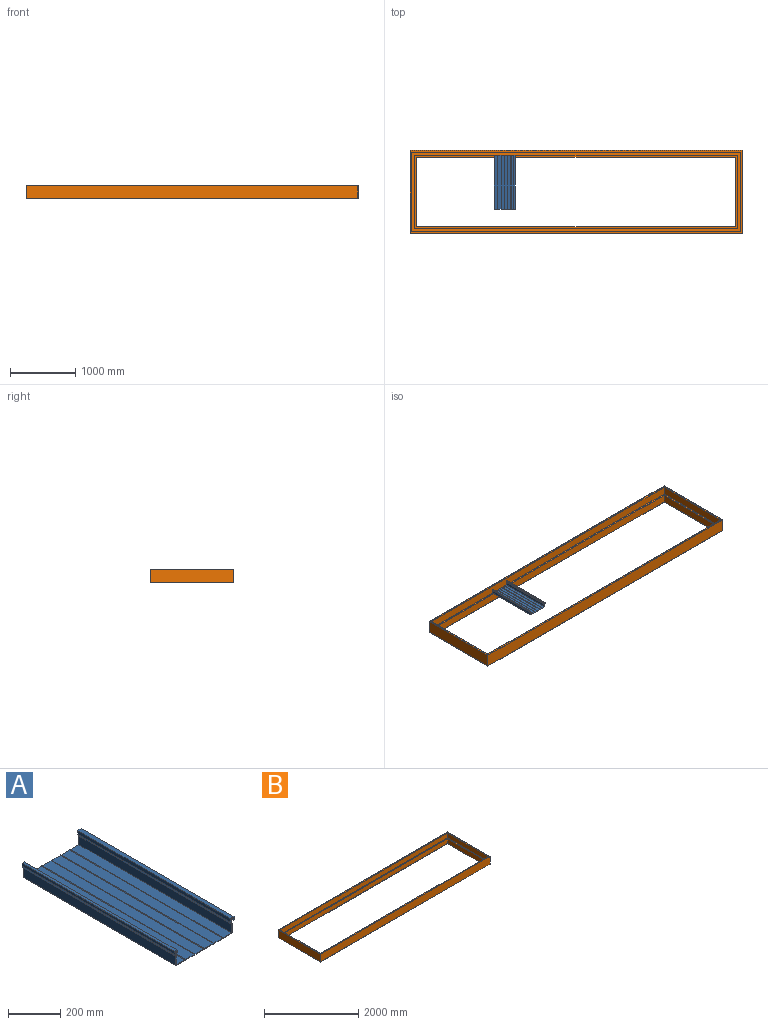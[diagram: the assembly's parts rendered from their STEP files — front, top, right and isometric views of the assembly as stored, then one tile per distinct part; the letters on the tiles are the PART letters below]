
ASSEMBLY  parts=2 mates=2
PART A: 58 faces, bbox 320.7x825.5x73 mm
  f0: plane 825.5x40.53mm, normal (-1,0,0), area 33453.8mm2, adj f1,f55,f56,f57
  f1: plane 825.5x46.04mm, normal (0,0,1), area 38004mm2, adj f0,f2,f56,f57
  f2: plane 825.5x1.59mm, normal (0.71,0,0.71), area 1853.3mm2, adj f1,f3,f56,f57
  f3: plane 825.5x1.59mm, normal (-0.71,0,0.71), area 1853.3mm2, adj f2,f4,f56,f57
  f4: plane 825.5x47.63mm, normal (0,0,1), area 39314.4mm2, adj f3,f5,f56,f57
  f5: plane 825.5x1.59mm, normal (0.71,0,0.71), area 1853.3mm2, adj f4,f6,f56,f57
  f6: plane 825.5x1.59mm, normal (-0.71,0,0.71), area 1853.3mm2, adj f5,f7,f56,f57
  f7: plane 825.5x47.63mm, normal (0,0,1), area 39314.4mm2, adj f6,f8,f56,f57
  f8: plane 825.5x1.59mm, normal (0.71,0,0.71), area 1853.3mm2, adj f7,f9,f56,f57
  f9: plane 825.5x1.59mm, normal (-0.71,0,0.71), area 1853.3mm2, adj f8,f10,f56,f57
  f10: plane 825.5x47.63mm, normal (0,0,1), area 39314.4mm2, adj f9,f11,f56,f57
  f11: plane 825.5x1.59mm, normal (0.71,0,0.71), area 1853.3mm2, adj f10,f12,f56,f57
  f12: plane 825.5x1.59mm, normal (-0.71,0,0.71), area 1853.3mm2, adj f11,f13,f56,f57
  f13: plane 825.5x47.63mm, normal (0,0,1), area 39314.4mm2, adj f12,f14,f56,f57
  f14: plane 825.5x1.59mm, normal (0.71,0,0.71), area 1853.3mm2, adj f13,f15,f56,f57
  f15: plane 825.5x1.59mm, normal (-0.71,0,0.71), area 1853.3mm2, adj f14,f16,f56,f57
  f16: plane 825.5x46.04mm, normal (0,0,1), area 38004mm2, adj f15,f17,f56,f57
  f17: plane 825.5x42.02mm, normal (1,0,0), area 34691.2mm2, adj f16,f18,f56,f57
  f18: plane 825.5x12.7mm, normal (0.89,0,0.45), area 11721.3mm2, adj f17,f19,f56,f57
  f19: plane 825.5x8.78mm, normal (1,0,0), area 7244.2mm2, adj f18,f20,f56,f57
  f20: plane 825.5x6.35mm, normal (0,0,-1), area 5241.9mm2, adj f19,f21,f56,f57
  f21: plane 825.5x9.53mm, normal (-1,0,0), area 7862.9mm2, adj f20,f22,f56,f57
  f22: plane 825.5x3.18mm, normal (0,0,-1), area 2621mm2, adj f21,f23,f56,f57
  f23: plane 825.5x12.7mm, normal (1,0,0), area 10483.8mm2, adj f22,f24,f56,f57
  f24: plane 825.5x12.7mm, normal (0,0,1), area 10483.8mm2, adj f23,f25,f56,f57
  f25: plane 825.5x12.7mm, normal (-1,0,0), area 10483.8mm2, adj f24,f26,f56,f57
  f26: plane 825.5x12.7mm, normal (-0.89,0,-0.45), area 11721.3mm2, adj f25,f27,f56,f57
  f27: plane 825.5x42.86mm, normal (-1,0,0), area 35383mm2, adj f26,f28,f56,f57
  f28: plane 825.5x1.59mm, normal (-0.71,0,-0.71), area 1853.3mm2, adj f27,f29,f56,f57
  f29: plane 825.5x47.63mm, normal (0,0,-1), area 39314.4mm2, adj f28,f30,f56,f57
  f30: plane 825.5x1.59mm, normal (0.71,0,-0.71), area 1853.3mm2, adj f29,f31,f56,f57
  f31: plane 825.5x1.59mm, normal (-0.71,0,-0.71), area 1853.3mm2, adj f30,f32,f56,f57
  f32: plane 825.5x47.63mm, normal (0,0,-1), area 39314.4mm2, adj f31,f33,f56,f57
  f33: plane 825.5x1.59mm, normal (0.71,0,-0.71), area 1853.3mm2, adj f32,f34,f56,f57
  f34: plane 825.5x1.59mm, normal (-0.71,0,-0.71), area 1853.3mm2, adj f33,f35,f56,f57
  f35: plane 825.5x47.63mm, normal (0,0,-1), area 39314.4mm2, adj f34,f36,f56,f57
  f36: plane 825.5x1.59mm, normal (0.71,0,-0.71), area 1853.3mm2, adj f35,f37,f56,f57
  f37: plane 825.5x1.59mm, normal (-0.71,0,-0.71), area 1853.3mm2, adj f36,f38,f56,f57
  f38: plane 825.5x47.63mm, normal (0,0,-1), area 39314.4mm2, adj f37,f39,f56,f57
  f39: plane 825.5x1.59mm, normal (0.71,0,-0.71), area 1853.3mm2, adj f38,f40,f56,f57
  f40: plane 825.5x1.59mm, normal (-0.71,0,-0.71), area 1853.3mm2, adj f39,f41,f56,f57
  f41: plane 825.5x47.63mm, normal (0,0,-1), area 39314.4mm2, adj f40,f42,f56,f57
  f42: plane 825.5x1.59mm, normal (0.71,0,-0.71), area 1853.3mm2, adj f41,f43,f56,f57
  f43: plane 825.5x1.59mm, normal (-0.71,0,-0.71), area 1853.3mm2, adj f42,f44,f56,f57
  f44: plane 825.5x47.63mm, normal (0,0,-1), area 39314.4mm2, adj f43,f45,f56,f57
  f45: plane 825.5x1.59mm, normal (0.71,0,-0.71), area 1853.3mm2, adj f44,f46,f56,f57
  f46: plane 825.5x42.86mm, normal (1,0,0), area 35383mm2, adj f45,f47,f56,f57
  f47: plane 825.5x12.7mm, normal (0.89,0,0.45), area 11721.3mm2, adj f46,f48,f56,f57
  f48: plane 825.5x12.7mm, normal (1,0,0), area 10483.8mm2, adj f47,f49,f56,f57
  f49: plane 825.5x12.7mm, normal (0,0,-1), area 10483.8mm2, adj f48,f50,f56,f57
  f50: plane 825.5x12.7mm, normal (-1,0,0), area 10483.8mm2, adj f49,f51,f56,f57
  f51: plane 825.5x3.18mm, normal (0,0,-1), area 2621mm2, adj f50,f52,f56,f57
  f52: plane 825.5x15.88mm, normal (1,0,0), area 13104.8mm2, adj f51,f53,f56,f57
  f53: plane 825.5x19.05mm, normal (0,0,1), area 15725.8mm2, adj f52,f54,f56,f57
  f54: plane 825.5x16.62mm, normal (-1,0,0), area 13723.5mm2, adj f53,f55,f56,f57
  f55: plane 825.5x12.7mm, normal (-0.89,0,-0.45), area 11721.3mm2, adj f0,f54,f56,f57
  f56: plane 320.68x73.03mm, normal (0,-1,0), area 1559.4mm2, adj f0,f1,f2,f3,f4,f5,f6,f7
  f57: plane 320.68x73.03mm, normal (0,1,0), area 1559.4mm2, adj f0,f1,f2,f3,f4,f5,f6,f7
PART B: 30 faces, bbox 5080x1270x203.2 mm
  f0: plane 1263.65x196.85mm, normal (1,0,0), area 248749.5mm2, adj f1,f7,f17,f24
  f1: plane 5073.65x196.85mm, normal (0,-1,0), area 998748mm2, adj f0,f2,f17,f24
  f2: plane 1263.65x196.85mm, normal (-1,0,0), area 248749.5mm2, adj f1,f7,f17,f24
  f3: plane 5080x203.2mm, normal (0,1,0), area 1032256mm2, adj f4,f6,f8,f29
  f4: plane 1270x203.2mm, normal (-1,0,0), area 258064mm2, adj f3,f5,f8,f29
  f5: plane 5080x203.2mm, normal (0,-1,0), area 1032256mm2, adj f4,f6,f8,f29
  f6: plane 1270x203.2mm, normal (1,0,0), area 258064mm2, adj f3,f5,f8,f29
  f7: plane 5073.65x196.85mm, normal (0,1,0), area 998748mm2, adj f0,f2,f17,f24
  f8: plane 5080x1270mm, normal (0,0,-1), area 1249029.8mm2, adj f3,f4,f5,f6,f9,f10,f11,f16
  f9: plane 1066.8x127mm, normal (1,0,0), area 135483.6mm2, adj f8,f10,f16,f22
  f10: plane 4876.8x127mm, normal (0,-1,0), area 619353.6mm2, adj f8,f9,f11,f22
  f11: plane 1066.8x127mm, normal (-1,0,0), area 135483.6mm2, adj f8,f10,f16,f22
  f12: plane 4883.15x120.65mm, normal (0,1,0), area 589152mm2, adj f13,f15,f17,f23
  f13: plane 1073.15x120.65mm, normal (-1,0,0), area 129475.5mm2, adj f12,f14,f17,f23
  f14: plane 4883.15x120.65mm, normal (0,-1,0), area 589152mm2, adj f13,f15,f17,f23
  f15: plane 1073.15x120.65mm, normal (1,0,0), area 129475.5mm2, adj f12,f14,f17,f23
  f16: plane 4876.8x127mm, normal (0,1,0), area 619353.6mm2, adj f8,f9,f11,f22
  f17: plane 5073.65x1263.65mm, normal (0,0,1), area 1170965.4mm2, adj f0,f1,f2,f7,f12,f13,f14,f15
  f18: plane 1117.6x3.18mm, normal (1,0,0), area 3548.4mm2, adj f19,f21,f22,f23
  f19: plane 4927.6x3.18mm, normal (0,1,0), area 15645.1mm2, adj f18,f20,f22,f23
  f20: plane 1117.6x3.18mm, normal (-1,0,0), area 3548.4mm2, adj f19,f21,f22,f23
  f21: plane 4927.6x3.18mm, normal (0,-1,0), area 15645.1mm2, adj f18,f20,f22,f23
  f22: plane 4927.6x1117.6mm, normal (0,0,1), area 304515.5mm2, adj f9,f10,f11,f16,f18,f19,f20,f21
  f23: plane 4927.6x1117.6mm, normal (0,0,-1), area 266733.3mm2, adj f12,f13,f14,f15,f18,f19,f20,f21
  f24: plane 5073.65x1263.65mm, normal (0,0,-1), area 279717.2mm2, adj f0,f1,f2,f7,f25,f26,f27,f28
  f25: plane 1219.2x3.18mm, normal (-1,0,0), area 3871mm2, adj f24,f26,f28,f29
  f26: plane 5029.2x3.18mm, normal (0,1,0), area 15967.7mm2, adj f24,f25,f27,f29
  f27: plane 1219.2x3.18mm, normal (1,0,0), area 3871mm2, adj f24,f26,f28,f29
  f28: plane 5029.2x3.18mm, normal (0,-1,0), area 15967.7mm2, adj f24,f25,f27,f29
  f29: plane 5080x1270mm, normal (0,0,1), area 319999.4mm2, adj f3,f4,f5,f6,f25,f26,f27,f28
PLACE A t=(-143.33,701.2,26.43)mm
PLACE B t=(-1429.91,-492.6,-100.57)mm fixed
MATE planar A.f57 <-> B.f19  axis (0,1,0) through (13.83,701.2,29.6)mm
MATE planar A.f38 <-> B.f22  axis (0,0,-1) through (64.63,701.2,26.43)mm
